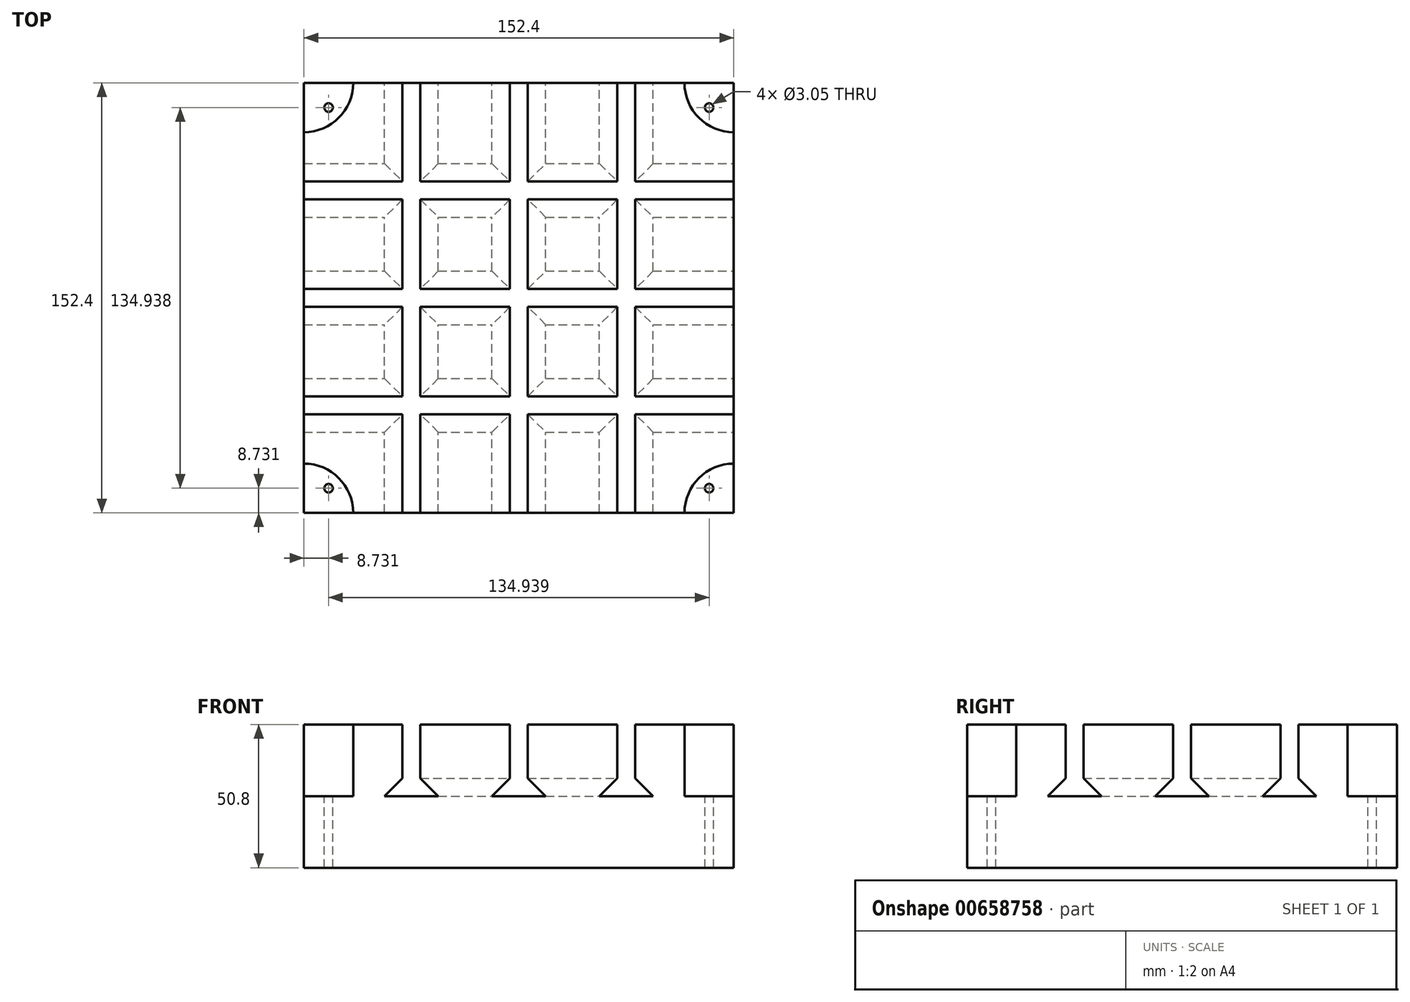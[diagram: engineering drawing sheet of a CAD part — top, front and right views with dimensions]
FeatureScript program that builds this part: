
annotation { "Feature Type Name" : "Feature", "Feature Type Description" : "" }
export const myFeature = defineFeature(function(context is Context, id is Id, definition is map)
    precondition{}
    {
        {
            var Q0;
            Q0=qCreatedBy(makeId("Front.planeOp"),FACE);
            var sketch = newSketch(context, id + "F0", { "sketchPlane" : qUnion([Q0])});
            skLineSegment(sketch, "E0.bottom", {"start": v(-76.2, 25.4) * mm, "end": v(76.2, 25.4) * mm});
            skLineSegment(sketch, "E0.top", {"start": v(-76.2, -25.4) * mm, "end": v(76.2, -25.4) * mm});
            skLineSegment(sketch, "E0.left", {"start": v(-76.2, 25.4) * mm, "end": v(-76.2, -25.4) * mm});
            skLineSegment(sketch, "E0.right", {"start": v(76.2, 25.4) * mm, "end": v(76.2, -25.4) * mm});
            skPoint(sketch, "E0.middle", {"position": v(0, 0) * mm});
            skSolve(sketch);
        }
        {
            var Q0;
            Q0=makeQuery(id+"F0.imprint","IMPRINT",FACE,{"disambiguationData":[TD([[makeQuery(id+"F0.imprint","IMPRINT",EDGE,{"derivedFrom":sQuery(id+"F0.wireOp",EDGE,"E0.bottom")}),-1.0]])]});
            extrude(context, id + "F1", {"entities" : qUnion([Q0]), "depth" : 152.4 * mm, "offsetDistance" : 25.4 * mm});
        }
        {
            var Q0;
            Q0=makeQuery(id+"F1.opExtrude","SWEPT_FACE",FACE,{"disambiguationData":[OSD([sQuery(id+"F0.wireOp",EDGE,"E0.right")])]});
            var sketch = newSketch(context, id + "F2", { "sketchPlane" : qUnion([Q0])});
            skPoint(sketch, "E1.0", {"position": v(-76.2, 25.4) * mm});
            skPoint(sketch, "E2.0", {"position": v(-76.2, -25.4) * mm});
            skPoint(sketch, "E3.0", {"position": v(-152.4, 0) * mm});
            skPoint(sketch, "E4.0", {"position": v(0, 0) * mm});
            skLineSegment(sketch, "E5", {"start": v(-117.47, 25.4) * mm, "end": v(-117.47, 6.35) * mm});
            skLineSegment(sketch, "E6", {"start": v(-123.82, 0) * mm, "end": v(-104.77, 0) * mm});
            skLineSegment(sketch, "E7", {"start": v(-111.12, 6.35) * mm, "end": v(-111.12, 25.4) * mm});
            skLineSegment(sketch, "E8", {"start": v(-111.12, 25.4) * mm, "end": v(-117.47, 25.4) * mm});
            skLineSegment(sketch, "E9", {"start": v(-76.2, 25.4) * mm, "end": v(-76.2, -25.4) * mm, "construction": true});
            skLineSegment(sketch, "E10.MirrorCS", {"start": v(-41.28, 25.4) * mm, "end": v(-34.93, 25.4) * mm});
            skLineSegment(sketch, "E11.MirrorCS", {"start": v(-41.28, 6.35) * mm, "end": v(-41.28, 25.4) * mm});
            skLineSegment(sketch, "E12.MirrorCS", {"start": v(-34.93, 25.4) * mm, "end": v(-34.93, 6.35) * mm});
            skLineSegment(sketch, "E13.MirrorCS", {"start": v(-28.58, 0) * mm, "end": v(-47.63, 0) * mm});
            skLineSegment(sketch, "E14", {"start": v(-79.38, 25.4) * mm, "end": v(-79.38, 6.35) * mm});
            skLineSegment(sketch, "E15", {"start": v(-85.72, 0) * mm, "end": v(-66.68, 0) * mm});
            skLineSegment(sketch, "E16", {"start": v(-73.03, 6.35) * mm, "end": v(-73.03, 25.4) * mm});
            skLineSegment(sketch, "E17", {"start": v(-73.03, 25.4) * mm, "end": v(-79.38, 25.4) * mm});
            skLineSegment(sketch, "E18", {"start": v(-117.47, 6.35) * mm, "end": v(-123.82, 0) * mm});
            skLineSegment(sketch, "E19", {"start": v(-111.12, 6.35) * mm, "end": v(-104.77, 0) * mm});
            skLineSegment(sketch, "E20", {"start": v(-85.72, 0) * mm, "end": v(-79.38, 6.35) * mm});
            skLineSegment(sketch, "E21", {"start": v(-73.03, 6.35) * mm, "end": v(-66.68, 0) * mm});
            skLineSegment(sketch, "E22", {"start": v(-47.63, 0) * mm, "end": v(-41.28, 6.35) * mm});
            skLineSegment(sketch, "E23", {"start": v(-34.93, 6.35) * mm, "end": v(-28.58, 0) * mm});
            skSolve(sketch);
        }
        {
            var Q0;
            Q0=qSketchRegion(id+"F2",true);
            extrude(context, id + "F3", {"entities" : qUnion([Q0]), "operationType" : NewBodyOperationType.REMOVE, "oppositeDirection" : true, "depth" : 203.2 * mm, "offsetDistance" : 25.4 * mm});
        }
        {
            var Q0;
            Q0=makeQuery(id+"F1.opExtrude","CAP_FACE",FACE,{"disambiguationData":[OSD([sQuery(id+"F0.wireOp",EDGE,"E0.bottom"),sQuery(id+"F0.wireOp",EDGE,"E0.top"),sQuery(id+"F0.wireOp",EDGE,"E0.left"),sQuery(id+"F0.wireOp",EDGE,"E0.right")])],"isStart":true});
            var sketch = newSketch(context, id + "F4", { "sketchPlane" : qUnion([Q0])});
            skLineSegment(sketch, "E24", {"start": v(-41.27, 25.4) * mm, "end": v(-41.27, 6.35) * mm});
            skLineSegment(sketch, "E25", {"start": v(-47.62, 0) * mm, "end": v(-28.57, 0) * mm});
            skLineSegment(sketch, "E26", {"start": v(-34.93, 6.35) * mm, "end": v(-34.93, 25.4) * mm});
            skLineSegment(sketch, "E27", {"start": v(-34.92, 25.4) * mm, "end": v(-41.27, 25.4) * mm});
            skLineSegment(sketch, "E28", {"start": v(0, 25.4) * mm, "end": v(0, -25.4) * mm, "construction": true});
            skLineSegment(sketch, "E29.MirrorCS", {"start": v(34.92, 25.4) * mm, "end": v(41.27, 25.4) * mm});
            skLineSegment(sketch, "E30.MirrorCS", {"start": v(47.62, 0) * mm, "end": v(28.57, 0) * mm});
            skLineSegment(sketch, "E31.MirrorCS", {"start": v(41.27, 25.4) * mm, "end": v(41.27, 6.35) * mm});
            skLineSegment(sketch, "E32.MirrorCS", {"start": v(34.92, 6.35) * mm, "end": v(34.92, 25.4) * mm});
            skLineSegment(sketch, "E33", {"start": v(-3.17, 25.4) * mm, "end": v(-3.17, 6.35) * mm});
            skLineSegment(sketch, "E34", {"start": v(-9.53, 0) * mm, "end": v(9.52, 0) * mm});
            skLineSegment(sketch, "E35", {"start": v(3.18, 6.35) * mm, "end": v(3.18, 25.4) * mm});
            skLineSegment(sketch, "E36", {"start": v(3.18, 25.4) * mm, "end": v(-3.17, 25.4) * mm});
            skPoint(sketch, "E37.0", {"position": v(-76.2, 25.4) * mm});
            skLineSegment(sketch, "E38", {"start": v(-41.27, 6.35) * mm, "end": v(-47.62, 0) * mm});
            skLineSegment(sketch, "E39", {"start": v(-34.93, 6.35) * mm, "end": v(-28.57, 0) * mm});
            skLineSegment(sketch, "E40", {"start": v(-9.53, 0) * mm, "end": v(-3.17, 6.35) * mm});
            skLineSegment(sketch, "E41", {"start": v(3.18, 6.35) * mm, "end": v(9.52, 0) * mm});
            skLineSegment(sketch, "E42", {"start": v(34.92, 6.35) * mm, "end": v(28.57, 0) * mm});
            skLineSegment(sketch, "E43", {"start": v(41.27, 6.35) * mm, "end": v(47.62, 0) * mm});
            skSolve(sketch);
        }
        {
            var Q0;
            Q0=qSketchRegion(id+"F4",true);
            extrude(context, id + "F5", {"entities" : qUnion([Q0]), "operationType" : NewBodyOperationType.REMOVE, "oppositeDirection" : true, "depth" : 203.2 * mm, "offsetDistance" : 25.4 * mm});
        }
        {
            var Q0;
            {var subQ1=sQuery(id+"F0.wireOp",EDGE,"E0.left");var subQ2=sQuery(id+"F0.wireOp",EDGE,"E0.bottom");var subQ4=makeQuery(id+"F1.opExtrude","SWEPT_FACE",FACE,{"disambiguationData":[OSD([subQ1])]});var subQ5=makeQuery(id+"F3.opExtrude","SWEPT_FACE",FACE,{"disambiguationData":[OSD([sQuery(id+"F2.wireOp",EDGE,"E12.MirrorCS")])]});Q0=makeQuery(id+"F5.boolean.opBoolean","SPLIT",FACE,{"disambiguationData":[TD([subQ4])],"derivedFrom":makeQuery(id+"F3.boolean.opBoolean","SPLIT",FACE,{"disambiguationData":[TD([subQ5])],"derivedFrom":makeQuery(id+"F1.opExtrude","SWEPT_FACE",FACE,{"disambiguationData":[OSD([subQ2])]})})});}
            var sketch = newSketch(context, id + "F6", { "sketchPlane" : qUnion([Q0])});
            skArc(sketch, "E44", {"start": v(-76.2, -17.46) * mm, "mid": v(-63.85, -12.35) * mm, "end": v(-58.74, 0) * mm});
            skLineSegment(sketch, "E45", {"start": v(-76.2, -17.46) * mm, "end": v(-76.2, 0) * mm});
            skSolve(sketch);
        }
        {
            var Q0;
            Q0=qSketchRegion(id+"F6",true);
            var Q1;
            {var subQ0=sQuery(id+"F6.wireOp",EDGE,"E44");Q1=makeQuery(id+"F6.imprint","IMPRINT",FACE,{"disambiguationData":[TD([[makeQuery(id+"F6.imprint","IMPRINT",EDGE,{"derivedFrom":subQ0}),1.0]])]});}
            extrude(context, id + "F7", {"entities" : qUnion([Q0, Q1]), "operationType" : NewBodyOperationType.REMOVE, "oppositeDirection" : true, "depth" : 25.4 * mm, "offsetDistance" : 25.4 * mm});
        }
        {
            var Q0;
            Q0=makeQuery(id+"F7.boolean.opBoolean","COPY",FACE,{"derivedFrom":makeQuery(id+"F7.opExtrude","CAP_FACE",FACE,{"disambiguationData":[OSD([sQuery(id+"F0.wireOp",EDGE,"E0.bottom"),sQuery(id+"F6.wireOp",EDGE,"E44"),sQuery(id+"F6.wireOp",EDGE,"E45")])],"isStart":false})});
            var sketch = newSketch(context, id + "F8", { "sketchPlane" : qUnion([Q0])});
            skCircle(sketch, "E46", {"center": v(-67.47, -8.73) * mm, "radius": 1.52 * mm});
            skPoint(sketch, "E46.centerSnap0", {"position": v(-67.47, 0) * mm});
            skSolve(sketch);
        }
        {
            var Q0;
            Q0=qSketchRegion(id+"F8",true);
            extrude(context, id + "F9", {"entities" : qUnion([Q0]), "operationType" : NewBodyOperationType.REMOVE, "oppositeDirection" : true, "depth" : 25.4 * mm, "offsetDistance" : 25.4 * mm});
        }
        {
            var Q0;
            {var subQ0=sQuery(id+"F0.wireOp",EDGE,"E0.right");var subQ2=sQuery(id+"F0.wireOp",EDGE,"E0.bottom");var subQ4=makeQuery(id+"F1.opExtrude","SWEPT_FACE",FACE,{"disambiguationData":[OSD([subQ0])]});var subQ5=makeQuery(id+"F3.opExtrude","SWEPT_FACE",FACE,{"disambiguationData":[OSD([sQuery(id+"F2.wireOp",EDGE,"E12.MirrorCS")])]});Q0=makeQuery(id+"F5.boolean.opBoolean","SPLIT",FACE,{"disambiguationData":[TD([subQ4])],"derivedFrom":makeQuery(id+"F3.boolean.opBoolean","SPLIT",FACE,{"disambiguationData":[TD([subQ5])],"derivedFrom":makeQuery(id+"F1.opExtrude","SWEPT_FACE",FACE,{"disambiguationData":[OSD([subQ2])]})})});}
            var sketch = newSketch(context, id + "F10", { "sketchPlane" : qUnion([Q0])});
            skArc(sketch, "E47", {"start": v(76.2, -17.46) * mm, "mid": v(63.85, -12.35) * mm, "end": v(58.74, 0) * mm});
            skLineSegment(sketch, "E48", {"start": v(76.2, 0) * mm, "end": v(76.2, -17.46) * mm});
            skLineSegment(sketch, "E49", {"start": v(76.2, 0) * mm, "end": v(58.74, 0) * mm});
            skSolve(sketch);
        }
        {
            var Q0;
            Q0=qSketchRegion(id+"F10",true);
            extrude(context, id + "F11", {"entities" : qUnion([Q0]), "operationType" : NewBodyOperationType.REMOVE, "oppositeDirection" : true, "depth" : 25.4 * mm, "offsetDistance" : 25.4 * mm});
        }
        {
            var Q0;
            Q0=makeQuery(id+"F11.boolean.opBoolean","COPY",FACE,{"derivedFrom":makeQuery(id+"F11.opExtrude","CAP_FACE",FACE,{"disambiguationData":[OSD([sQuery(id+"F10.wireOp",EDGE,"E47"),sQuery(id+"F10.wireOp",EDGE,"E48"),sQuery(id+"F10.wireOp",EDGE,"E49")])],"isStart":false})});
            var sketch = newSketch(context, id + "F12", { "sketchPlane" : qUnion([Q0])});
            skPoint(sketch, "E50.0", {"position": v(76.2, -8.73) * mm});
            skPoint(sketch, "E51.0", {"position": v(67.47, 0) * mm});
            skCircle(sketch, "E52", {"center": v(67.47, -8.73) * mm, "radius": 1.52 * mm});
            skSolve(sketch);
        }
        {
            var Q0;
            Q0=qSketchRegion(id+"F12",true);
            extrude(context, id + "F13", {"entities" : qUnion([Q0]), "operationType" : NewBodyOperationType.REMOVE, "oppositeDirection" : true, "depth" : 25.4 * mm, "offsetDistance" : 25.4 * mm});
        }
        {
            var Q0;
            {var subQ0=sQuery(id+"F0.wireOp",EDGE,"E0.right");var subQ2=sQuery(id+"F0.wireOp",EDGE,"E0.bottom");var subQ4=makeQuery(id+"F1.opExtrude","SWEPT_FACE",FACE,{"disambiguationData":[OSD([subQ0])]});var subQ5=makeQuery(id+"F3.opExtrude","SWEPT_FACE",FACE,{"disambiguationData":[OSD([sQuery(id+"F2.wireOp",EDGE,"E5")])]});Q0=makeQuery(id+"F5.boolean.opBoolean","SPLIT",FACE,{"disambiguationData":[TD([subQ4])],"derivedFrom":makeQuery(id+"F3.boolean.opBoolean","SPLIT",FACE,{"disambiguationData":[TD([subQ5])],"derivedFrom":makeQuery(id+"F1.opExtrude","SWEPT_FACE",FACE,{"disambiguationData":[OSD([subQ2])]})})});}
            var sketch = newSketch(context, id + "F14", { "sketchPlane" : qUnion([Q0])});
            skArc(sketch, "E53", {"start": v(58.74, -152.4) * mm, "mid": v(63.85, -140.05) * mm, "end": v(76.2, -134.94) * mm});
            skLineSegment(sketch, "E54", {"start": v(76.2, -152.4) * mm, "end": v(58.74, -152.4) * mm});
            skLineSegment(sketch, "E55", {"start": v(76.2, -152.4) * mm, "end": v(76.2, -134.94) * mm});
            skSolve(sketch);
        }
        {
            var Q0;
            Q0=qSketchRegion(id+"F14",true);
            extrude(context, id + "F15", {"entities" : qUnion([Q0]), "operationType" : NewBodyOperationType.REMOVE, "oppositeDirection" : true, "depth" : 25.4 * mm, "offsetDistance" : 25.4 * mm});
        }
        {
            var Q0;
            Q0=makeQuery(id+"F15.boolean.opBoolean","COPY",FACE,{"derivedFrom":makeQuery(id+"F15.opExtrude","CAP_FACE",FACE,{"disambiguationData":[OSD([sQuery(id+"F14.wireOp",EDGE,"E53"),sQuery(id+"F14.wireOp",EDGE,"E54"),sQuery(id+"F14.wireOp",EDGE,"E55")])],"isStart":false})});
            var sketch = newSketch(context, id + "F16", { "sketchPlane" : qUnion([Q0])});
            skPoint(sketch, "E56.0", {"position": v(76.2, -143.67) * mm});
            skPoint(sketch, "E57.0", {"position": v(67.47, -152.4) * mm});
            skCircle(sketch, "E58", {"center": v(67.47, -143.67) * mm, "radius": 1.52 * mm});
            skSolve(sketch);
        }
        {
            var Q0;
            Q0=qSketchRegion(id+"F16",true);
            extrude(context, id + "F17", {"entities" : qUnion([Q0]), "operationType" : NewBodyOperationType.REMOVE, "oppositeDirection" : true, "depth" : 25.4 * mm, "offsetDistance" : 25.4 * mm});
        }
        {
            var Q0;
            {var subQ1=sQuery(id+"F0.wireOp",EDGE,"E0.left");var subQ2=sQuery(id+"F0.wireOp",EDGE,"E0.bottom");var subQ4=makeQuery(id+"F1.opExtrude","SWEPT_FACE",FACE,{"disambiguationData":[OSD([subQ1])]});var subQ5=makeQuery(id+"F3.opExtrude","SWEPT_FACE",FACE,{"disambiguationData":[OSD([sQuery(id+"F2.wireOp",EDGE,"E5")])]});Q0=makeQuery(id+"F5.boolean.opBoolean","SPLIT",FACE,{"disambiguationData":[TD([subQ4])],"derivedFrom":makeQuery(id+"F3.boolean.opBoolean","SPLIT",FACE,{"disambiguationData":[TD([subQ5])],"derivedFrom":makeQuery(id+"F1.opExtrude","SWEPT_FACE",FACE,{"disambiguationData":[OSD([subQ2])]})})});}
            var sketch = newSketch(context, id + "F18", { "sketchPlane" : qUnion([Q0])});
            skArc(sketch, "E59", {"start": v(-76.2, -134.94) * mm, "mid": v(-63.85, -140.05) * mm, "end": v(-58.74, -152.4) * mm});
            skLineSegment(sketch, "E60", {"start": v(-76.2, -152.4) * mm, "end": v(-58.74, -152.4) * mm});
            skLineSegment(sketch, "E61", {"start": v(-76.2, -152.4) * mm, "end": v(-76.2, -134.94) * mm});
            skSolve(sketch);
        }
        {
            var Q0;
            Q0=qSketchRegion(id+"F18",true);
            extrude(context, id + "F19", {"entities" : qUnion([Q0]), "operationType" : NewBodyOperationType.REMOVE, "oppositeDirection" : true, "depth" : 25.4 * mm, "offsetDistance" : 25.4 * mm});
        }
        {
            var Q0;
            Q0=makeQuery(id+"F19.boolean.opBoolean","COPY",FACE,{"derivedFrom":makeQuery(id+"F19.opExtrude","CAP_FACE",FACE,{"disambiguationData":[OSD([sQuery(id+"F18.wireOp",EDGE,"E59"),sQuery(id+"F18.wireOp",EDGE,"E60"),sQuery(id+"F18.wireOp",EDGE,"E61")])],"isStart":false})});
            var sketch = newSketch(context, id + "F20", { "sketchPlane" : qUnion([Q0])});
            skPoint(sketch, "E62.0", {"position": v(-76.2, -143.67) * mm});
            skPoint(sketch, "E63.0", {"position": v(-67.47, -152.4) * mm});
            skCircle(sketch, "E64", {"center": v(-67.47, -143.67) * mm, "radius": 1.52 * mm});
            skSolve(sketch);
        }
        {
            var Q0;
            Q0=qSketchRegion(id+"F20",true);
            extrude(context, id + "F21", {"entities" : qUnion([Q0]), "operationType" : NewBodyOperationType.REMOVE, "oppositeDirection" : true, "depth" : 25.4 * mm, "offsetDistance" : 25.4 * mm});
        }
    });
